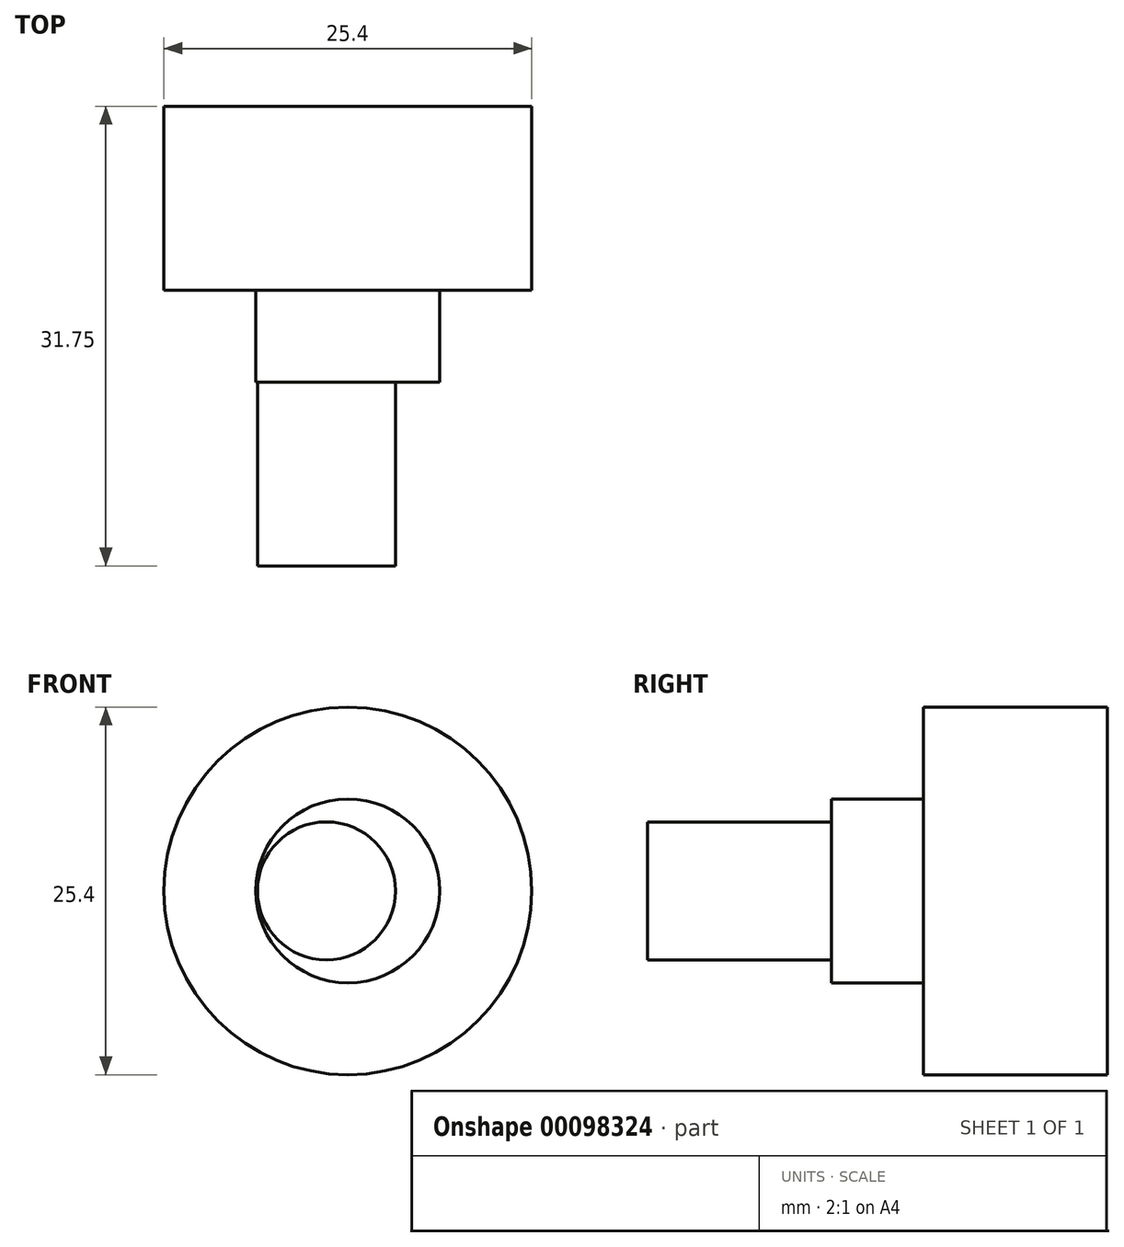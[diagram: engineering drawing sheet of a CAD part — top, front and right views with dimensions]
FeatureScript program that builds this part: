
annotation { "Feature Type Name" : "Feature", "Feature Type Description" : "" }
export const myFeature = defineFeature(function(context is Context, id is Id, definition is map)
    precondition{}
    {
        {
            var Q0;
            Q0=qCreatedBy(makeId("Front.planeOp"),FACE);
            var sketch = newSketch(context, id + "F0", { "sketchPlane" : qUnion([Q0])});
            skCircle(sketch, "E0", {"center": v(0, 0) * mm, "radius": 12.7 * mm});
            skCircle(sketch, "E1", {"center": v(0, 0) * mm, "radius": 6.35 * mm});
            skCircle(sketch, "E2", {"center": v(-1.48, 0) * mm, "radius": 4.76 * mm});
            skSolve(sketch);
        }
        {
            var Q0;
            Q0 = qSketchRegion(id + "F0", true);
            var Q1;
            Q1=makeQuery(id+"F0.imprint","IMPRINT",FACE,{"disambiguationData":[TD([[makeQuery(id+"F0.imprint","IMPRINT",EDGE,{"derivedFrom":sQuery(id+"F0.wireOp",EDGE,"E2")}),1.0]])]});
            var Q2;
            Q2=makeQuery(id+"F0.imprint","IMPRINT",FACE,{"disambiguationData":[TD([[makeQuery(id+"F0.imprint","IMPRINT",EDGE,{"derivedFrom":sQuery(id+"F0.wireOp",EDGE,"E1")}),1.0]])]});
            extrude(context, id + "F1", {"entities" : qUnion([Q0, Q1, Q2]), "depth" : 12.7 * mm});
        }
        {
            var Q0;
            Q0=makeQuery(id+"F0.imprint","IMPRINT",FACE,{"disambiguationData":[TD([[makeQuery(id+"F0.imprint","IMPRINT",EDGE,{"derivedFrom":sQuery(id+"F0.wireOp",EDGE,"E2")}),1.0]])]});
            var Q1;
            Q1=makeQuery(id+"F0.imprint","IMPRINT",FACE,{"disambiguationData":[TD([[makeQuery(id+"F0.imprint","IMPRINT",EDGE,{"derivedFrom":sQuery(id+"F0.wireOp",EDGE,"E1")}),1.0]])]});
            extrude(context, id + "F2", {"entities" : qUnion([Q0, Q1]), "operationType" : NewBodyOperationType.ADD, "depth" : 19.05 * mm});
        }
        {
            var Q0;
            Q0=makeQuery(id+"F0.imprint","IMPRINT",FACE,{"disambiguationData":[TD([[makeQuery(id+"F0.imprint","IMPRINT",EDGE,{"derivedFrom":sQuery(id+"F0.wireOp",EDGE,"E2")}),1.0]])]});
            extrude(context, id + "F3", {"entities" : qUnion([Q0]), "operationType" : NewBodyOperationType.ADD, "depth" : 31.75 * mm});
        }
    });
